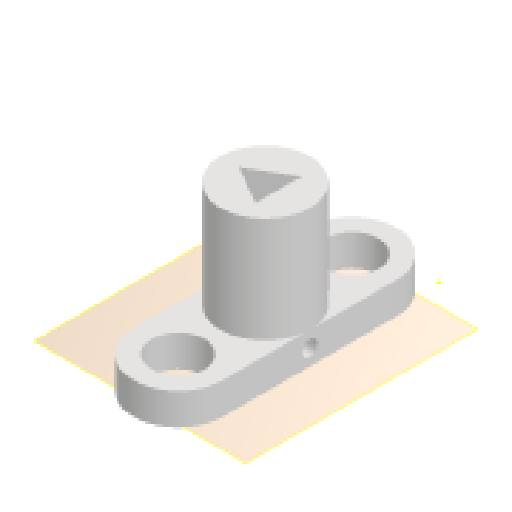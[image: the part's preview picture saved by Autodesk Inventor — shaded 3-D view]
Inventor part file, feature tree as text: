
AUTODESK INVENTOR PART (.ipt)
format: ipt  version: 2024.1 (Build 281209000, 209)  size: 142,336 bytes
history: native  units: mm
features: sketch x4, extrude x3, other x3, plane x1, reference x1, projected_geometry x1
ambient origin geometry x8: Origin, YZ Plane, XZ Plane, XY Plane, X Axis, Y Axis, Z Axis, Center Point
bodies: Volumenkörper1 (feature_tree)
feature tree (13):
  plane  "Arbeitsebene1"
  extrude  "Extrusion1"  Depth=10.0mm
  extrude  "Extrusion2"  Depth=17.0mm
  sketch  "Skizze3"  dims[d4=6.0mm d5=0.0mm d6=2.8mm]
  extrude  "Extrusion3"  Depth=6.0mm
  sketch  "Skizze1"  dims[d0=10.0mm d1=10.0mm]
  reference  "Referenz1"
  sketch  "Skizze2"  dims[d2=5.0mm d3=17.0mm]
  sketch  "Skizze4"  dims[d7=0.0mm d8=0.0mm d9=5.0mm d10=20.0mm d11=0.0mm]
  projected_geometry  "Projizierte Kontur1"
  other  "Application_Investigator_Lighsheet.iam"
  other  "40_XYZstage_micrometer_motorized_nema8_samplemount_lightsheet_screwed:1"
  other  "Baugruppe2"
